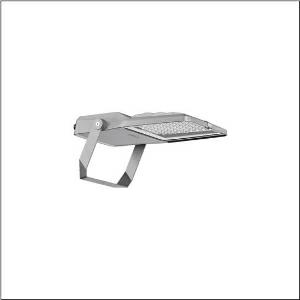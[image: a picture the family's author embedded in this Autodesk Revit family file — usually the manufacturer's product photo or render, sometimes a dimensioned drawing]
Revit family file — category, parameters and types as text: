
# Revit family: floodlight_fl_21_iq_mini___pl64_5xa7771b2e1a_713d
name_source: partatom
category: Lighting Fixtures
units: mm (PartAtom-declared; Revit-internal decimal feet)

## family parameters
Cut with Voids When Loaded = No
Host = Face
Light Source = No
Part Type = Normal
Room Calculation Point = No
Round Connector Dimension = Use Diameter
Shared = No

## types (1)
- --- (1 x LED, 6020 lm, 45.5 W, 3000K)
    Apparent Load = 46 VA
    CIE Flux Codes = 28 80 98 100 100
    Color Rendering = 70
    Color Temperature = 3000K
    Default Elevation = 1800 mm
    Description = Floodlight FL 21 iQ mini, floodlight, primary light control with lens, of PMMA, primary optical cover: protective disc, of toughened safety glass, transparent, light distribution: PL64, light emission: direct distribution, installation type: surface-mounted, lamps: LED, High Power LED, rated values: 6.020lm | 45,5W | 132,3lm/W (begin service life); end service life: 6.020lm | 48W; at 50% lumin. flux: 3.010lm | 21,5W | 140lm/W, colour temperature: 3000K, colour rendering: CRI > 70, light colour: 730, light setting 1 begin service life: 100% | 6.020lm | 45,5W | 132,3lm/W | 3.000K, light setting 1 end service life: 48W, further light settings possible, control: Auto-Match, Temp-Guard, Lumen-Switch, Night-Set, Smart-Wire, Light-Fading, Desk-Remote (wireless, voltage-free reading and setting of iQ features in the workshop via application-optimized NFC function/RFID function), optimised constant luminous flux control (CLO 2.0), pre-setting: linear dimming characteristic, with terminal, 6-pole, mains connection: 220..240V, AC, 50/60Hz, luminaire housing, of diecast aluminium, powder-coated, SITECO metallic grey (DB 702S), corrosivity category C5 mid according to DIN EN ISO 12944suitable for swimming poolschlorine-resistant, sealing non-destructively replaceable, mounting bracket, of steel, galvanised, powder-coated, SITECO metallic grey (DB 702S), protection rating (complete): IP66, insulation class (complete): insulation class II (safety insulation), certification: CE, ENEC, VDE, protection symbol: D, impact resistance: IK08, permissible operating ambient temperature: -40..+40°C, permissible operating ambient temperature for outdoor applications: -40..+50°C, standard: DIN EN 12944, LABS conformity tested according to VDMA 24364:2018-05, packaging unit: 1 piece

Light Distribution: PL64
    Height = 70 mm
    Lamp = 1 x LED
    Lamp Light Flux = 6020 lm
    Lamp Power = 45.5 W
    Lamp count = 1
    Length = 485 mm
    Luminous efficacy = 132 lm/W
    Manufacturer = Siteco
    ModVariant = No
    Model = 5XA7771B2E1A
    Mounting Place = Wall
    Mounting Type = Surface mounted
    Number of Poles = 1
    OnlyDefault = Yes
    Power Factor = 1
    Product Name = Floodlight FL 21 iQ mini | PL64
    Product group = floodlight | wall mounted
    ProductGroupID = 2002
    Protection Class = Protection class II
    Protection Degree = IP 66
    RLX_Detail_Level = 1
    RLX_Emergency_Light_Flux = 0 lm
    RLX_Emergency_Type = 0
    RLX_Emergency_Type_DB = No
    RlxData = <blob elided: 96421 chars, md5=714e06ba>
    Socket = socket
    Standby Power = 0 W
    System Light Flux = 6020 lm
    System Power = 46 W
    Type Comments = factory setting: luminous flux: 100 % | dim-lin: 254 | 463 mA
    Type Image = l_1006845.jpg
    URL = http://relux.com
    VarID = @adj_166703
    Voltage = 0 V
    Weight = 0.00 kg
    Width = 337 mm

## geometry (parser evidence)
native form markers: Blend x4, Sweep x14
no freeform markers — native parametric forms only
